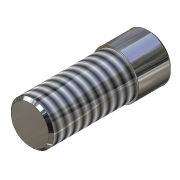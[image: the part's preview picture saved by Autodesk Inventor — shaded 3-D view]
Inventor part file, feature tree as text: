
AUTODESK INVENTOR PART (.ipt)
format: ipt  version: 2014 (Build 180170000, 170)  size: 122,368 bytes
history: native  units: mm (DEFAULTED — no unit token found)
features: extrude x2, chamfer x2, sketch x2, thread x1, reference x1
ambient origin geometry x8: Origin, YZ Plane, XZ Plane, XY Plane, X Axis, Y Axis, Z Axis, Center Point
bodies: Solid1 (feature_tree)
feature tree (8):
  extrude  "Extrusion1"  Depth=5.08mm TaperAngle=0.0deg
  chamfer  "Chamfer1"  Distance=3.175mm
  extrude  "Extrusion2"  Depth=12.7mm TaperAngle=0.0deg
  chamfer  "Chamfer2"  Distance=3.175mm
  thread  "Thread1"  [1 undecoded]
  sketch  "Sketch1"  dims[d0=6.858mm d1=5.08mm d2=0.0mm d3=0.381mm d4=3.175mm]
  reference  "Reference1"
  sketch  "Sketch2"  dims[d5=6.35mm d6=12.7mm d7=0.0mm d8=0.381mm d9=3.175mm d10=25.4mm d11=0.0mm d12=45.0deg d13=45.0deg]
note: 1 required parameter value undecoded (feature->parameter linkage not recoverable at this tier; creation-order binding heuristic only, values carry confidence <= 0.55)
